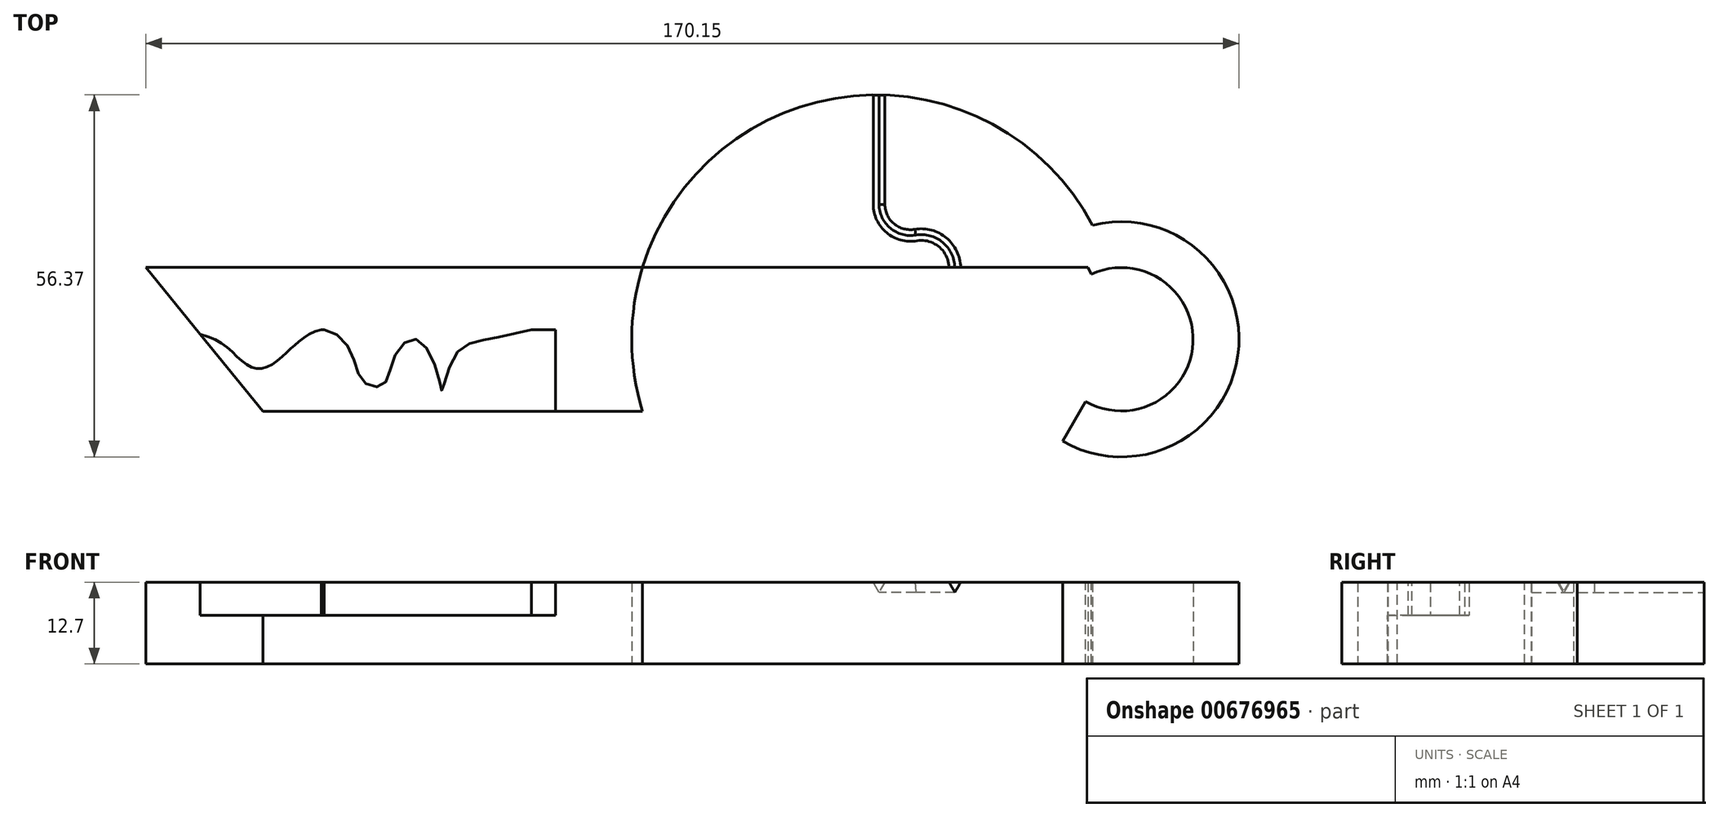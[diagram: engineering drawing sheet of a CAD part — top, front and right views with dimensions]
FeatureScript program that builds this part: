
annotation { "Feature Type Name" : "Feature", "Feature Type Description" : "" }
export const myFeature = defineFeature(function(context is Context, id is Id, definition is map)
    precondition{}
    {
        {
            var Q0;
            Q0=qCreatedBy(makeId("Top.planeOp"),FACE);
            var sketch = newSketch(context, id + "F0", { "sketchPlane" : qUnion([Q0])});
            skLineSegment(sketch, "E0", {"start": v(-76.55, 0) * mm, "end": v(76.12, 0) * mm});
            skLineSegment(sketch, "E1", {"start": v(0, 77.38) * mm, "end": v(0, -75.9) * mm});
            skLineSegment(sketch, "E2", {"start": v(0, 0) * mm, "end": v(76.12, 0) * mm});
            skLineSegment(sketch, "E3", {"start": v(38.06, 0) * mm, "end": v(38.06, 75.69) * mm});
            skCircle(sketch, "E4", {"center": v(38.06, 0) * mm, "radius": 38.06 * mm});
            skLineSegment(sketch, "E5.bottom", {"start": v(-75.64, 11.2) * mm, "end": v(74.43, 11.2) * mm});
            skLineSegment(sketch, "E5.top", {"start": v(-75.64, -11.2) * mm, "end": v(1.69, -11.2) * mm});
            skLineSegment(sketch, "E5.left", {"start": v(-75.64, 11.2) * mm, "end": v(-75.64, -11.2) * mm});
            skPoint(sketch, "E5.middle", {"position": v(0, 0) * mm});
            skSolve(sketch);
        }
        {
            var Q0;
            {var subQ0=sQuery(id+"F0.wireOp",EDGE,"E4");var subQ1=sQuery(id+"F0.wireOp",EDGE,"E3");var subQ2=makeQuery(id+"F0.imprint","INTERSECT",VERTEX,{"derivedFrom":[subQ1,subQ0]});Q0=makeQuery(id+"F0.imprint","IMPRINT",FACE,{"disambiguationData":[TD([[makeQuery(id+"F0.imprint","IMPRINT",EDGE,{"disambiguationData":[TD([[subQ2,1.0]])],"derivedFrom":subQ1}),1.0]])]});}
            var Q1;
            {var subQ0=sQuery(id+"F0.wireOp",EDGE,"E4");var subQ1=sQuery(id+"F0.wireOp",EDGE,"E3");var subQ2=makeQuery(id+"F0.imprint","INTERSECT",VERTEX,{"derivedFrom":[subQ1,subQ0]});Q1=makeQuery(id+"F0.imprint","IMPRINT",FACE,{"disambiguationData":[TD([[makeQuery(id+"F0.imprint","IMPRINT",EDGE,{"disambiguationData":[TD([[subQ2,1.0]])],"derivedFrom":subQ1}),-1.0]])]});}
            var Q2;
            {var subQ0=sQuery(id+"F0.wireOp",EDGE,"E4");var subQ1=sQuery(id+"F0.wireOp",EDGE,"E2");var subQ2=makeQuery(id+"F0.imprint","INTERSECT",VERTEX,{"derivedFrom":[subQ1,subQ0]});Q2=makeQuery(id+"F0.imprint","IMPRINT",FACE,{"disambiguationData":[TD([[makeQuery(id+"F0.imprint","IMPRINT",EDGE,{"disambiguationData":[TD([[subQ2,1.0]])],"derivedFrom":subQ1}),1.0]])]});}
            var Q3;
            {var subQ1=sQuery(id+"F0.wireOp",EDGE,"E2");var subQ3=sQuery(id+"F0.wireOp",EDGE,"E3");var subQ4=makeQuery(id+"F0.imprint","INTERSECT",VERTEX,{"derivedFrom":[subQ1,subQ3]});Q3=makeQuery(id+"F0.imprint","IMPRINT",FACE,{"disambiguationData":[TD([[makeQuery(id+"F0.imprint","IMPRINT",EDGE,{"disambiguationData":[TD([[subQ4,-1.0]])],"derivedFrom":subQ3}),1.0]])]});}
            var Q4;
            {var subQ0=sQuery(id+"F0.wireOp",EDGE,"E4");var subQ1=sQuery(id+"F0.wireOp",EDGE,"E2");var subQ4=makeQuery(id+"F0.imprint","INTERSECT",VERTEX,{"derivedFrom":[subQ1,subQ0]});Q4=makeQuery(id+"F0.imprint","IMPRINT",FACE,{"disambiguationData":[TD([[makeQuery(id+"F0.imprint","IMPRINT",EDGE,{"disambiguationData":[TD([[subQ4,1.0]])],"derivedFrom":subQ1}),-1.0]])]});}
            var Q5;
            {var subQ3=sQuery(id+"F0.wireOp",EDGE,"E5.left");var subQ5=sQuery(id+"F0.wireOp",EDGE,"E5.top");var subQ6=makeQuery(id+"F0.imprint","INTERSECT",VERTEX,{"derivedFrom":[subQ5,subQ3]});Q5=makeQuery(id+"F0.imprint","IMPRINT",FACE,{"disambiguationData":[TD([[makeQuery(id+"F0.imprint","IMPRINT",EDGE,{"disambiguationData":[TD([[subQ6,-1.0]])],"derivedFrom":subQ5}),1.0]])]});}
            var Q6;
            {var subQ3=sQuery(id+"F0.wireOp",EDGE,"E5.left");var subQ5=sQuery(id+"F0.wireOp",EDGE,"E5.bottom");var subQ7=makeQuery(id+"F0.imprint","INTERSECT",VERTEX,{"derivedFrom":[subQ5,subQ3]});Q6=makeQuery(id+"F0.imprint","IMPRINT",FACE,{"disambiguationData":[TD([[makeQuery(id+"F0.imprint","IMPRINT",EDGE,{"disambiguationData":[TD([[subQ7,-1.0]])],"derivedFrom":subQ5}),-1.0]])]});}
            var Q7;
            {var subQ1=sQuery(id+"F0.wireOp",EDGE,"E1");var subQ3=sQuery(id+"F0.wireOp",EDGE,"E5.bottom");var subQ4=makeQuery(id+"F0.imprint","INTERSECT",VERTEX,{"derivedFrom":[subQ1,subQ3]});Q7=makeQuery(id+"F0.imprint","IMPRINT",FACE,{"disambiguationData":[TD([[makeQuery(id+"F0.imprint","IMPRINT",EDGE,{"disambiguationData":[TD([[subQ4,-1.0]])],"derivedFrom":subQ3}),-1.0]])]});}
            var Q8;
            {var subQ0=sQuery(id+"F0.wireOp",EDGE,"E4");var subQ3=sQuery(id+"F0.wireOp",EDGE,"E5.top");var subQ5=makeQuery(id+"F0.imprint","INTERSECT",VERTEX,{"derivedFrom":[subQ0,subQ3]});Q8=makeQuery(id+"F0.imprint","IMPRINT",FACE,{"disambiguationData":[TD([[makeQuery(id+"F0.imprint","IMPRINT",EDGE,{"disambiguationData":[TD([[subQ5,1.0]])],"derivedFrom":subQ3}),1.0]])]});}
            extrude(context, id + "F1", {"entities" : qUnion([Q0, Q1, Q2, Q3, Q4, Q5, Q6, Q7, Q8]), "depth" : 12.7 * mm, "offsetDistance" : 25.4 * mm});
        }
        {
            var Q0;
            Q0=makeQuery(id+"F1.opExtrude","SWEPT_FACE",FACE,{"disambiguationData":[OSD([sQuery(id+"F0.wireOp",EDGE,"E5.top")])]});
            var sketch = newSketch(context, id + "F2", { "sketchPlane" : qUnion([Q0])});
            skPoint(sketch, "E6.oppositeSnap0", {"position": v(1.69, 6.35) * mm});
            skLineSegment(sketch, "E7.bottom", {"start": v(-75.64, 12.7) * mm, "end": v(-11.84, 12.7) * mm});
            skLineSegment(sketch, "E7.top", {"start": v(-75.64, 7.53) * mm, "end": v(-11.84, 7.53) * mm});
            skLineSegment(sketch, "E7.left", {"start": v(-75.64, 12.7) * mm, "end": v(-75.64, 7.53) * mm});
            skLineSegment(sketch, "E7.right", {"start": v(-11.84, 12.7) * mm, "end": v(-11.84, 7.53) * mm});
            skSolve(sketch);
        }
        {
            var Q0;
            Q0 = qSketchRegion(id + "F2", true);
            extrude(context, id + "F3", {"entities" : qUnion([Q0]), "operationType" : NewBodyOperationType.REMOVE, "oppositeDirection" : true, "depth" : 12.7 * mm, "offsetDistance" : 25.4 * mm});
        }
        {
            var Q0;
            Q0=makeQuery(id+"F3.boolean.opBoolean","COPY",FACE,{"derivedFrom":makeQuery(id+"F3.opExtrude","SWEPT_FACE",FACE,{"disambiguationData":[OSD([sQuery(id+"F2.wireOp",EDGE,"E7.top")])]})});
            var sketch = newSketch(context, id + "F4", { "sketchPlane" : qUnion([Q0])});
            skPoint(sketch, "E8.8.internal.snap0", {"position": v(-43.74, 1.5) * mm});
            skFitSpline(sketch, "E8", {"points": [v(-71.4, 1.5) * mm, v(-64.86, 0) * mm, v(-61.37, -2.73) * mm, v(-58.75, -4.47) * mm, v(-56.14, -4.03) * mm, v(-53.52, -1.85) * mm, v(-51.34, 0) * mm, v(-47.85, 1.5) * mm, v(-43.74, -1.85) * mm, v(-41.75, -6.65) * mm, v(-38.7, -7.09) * mm, v(-36.95, -2.73) * mm, v(-33.46, 0) * mm, v(-29.98, -6.21) * mm, v(-29.54, -7.96) * mm, v(-27.36, -2.29) * mm, v(-22.56, 0) * mm, v(-15.59, 1.5) * mm], "startDerivative": vector(98.42, -12.85) * mm, "endDerivative": vector(95.91, 21.9) * mm});
            skLineSegment(sketch, "E9", {"start": v(-71.4, 1.5) * mm, "end": v(-15.59, 1.5) * mm});
            skSolve(sketch);
        }
        {
            var Q0;
            {var subQ0=sQuery(id+"F4.wireOp",EDGE,"E9");var subQ1=sQuery(id+"F4.wireOp",EDGE,"E8");var subQ3=makeQuery(id+"F4.imprint","INTERSECT",VERTEX,{"disambiguationData":[OD(0.0)],"derivedFrom":[subQ1,subQ0]});Q0=makeQuery(id+"F4.imprint","IMPRINT",FACE,{"disambiguationData":[TD([[makeQuery(id+"F4.imprint","IMPRINT",EDGE,{"disambiguationData":[TD([[subQ3,1.0]])],"derivedFrom":subQ1}),1.0]])]});}
            var Q1;
            {var subQ0=sQuery(id+"F4.wireOp",EDGE,"E9");var subQ1=sQuery(id+"F4.wireOp",EDGE,"E8");var subQ3=makeQuery(id+"F4.imprint","INTERSECT",VERTEX,{"disambiguationData":[OD(1.0)],"derivedFrom":[subQ1,subQ0]});Q1=makeQuery(id+"F4.imprint","IMPRINT",FACE,{"disambiguationData":[TD([[makeQuery(id+"F4.imprint","IMPRINT",EDGE,{"disambiguationData":[TD([[subQ3,-1.0]])],"derivedFrom":subQ1}),1.0]])]});}
            var Q2;
            Q2=makeQuery(id+"F1.opExtrude","CAP_FACE",FACE,{"disambiguationData":[OSD([sQuery(id+"F0.wireOp",EDGE,"E4"),sQuery(id+"F0.wireOp",EDGE,"E5.bottom"),sQuery(id+"F0.wireOp",EDGE,"E5.top"),sQuery(id+"F0.wireOp",EDGE,"E5.left")])],"isStart":false});
            extrude(context, id + "F5", {"entities" : qUnion([Q0, Q1]), "operationType" : NewBodyOperationType.ADD, "endBound" : BoundingType.UP_TO_SURFACE, "depth" : 25.4 * mm, "endBoundEntityFace" : qUnion([Q2]), "offsetDistance" : 25.4 * mm});
        }
        {
            var Q0;
            {var subQ0=sQuery(id+"F0.wireOp",EDGE,"E5.left");var subQ1=sQuery(id+"F0.wireOp",EDGE,"E5.top");var subQ2=sQuery(id+"F0.wireOp",EDGE,"E5.bottom");var subQ3=sQuery(id+"F0.wireOp",EDGE,"E4");Q0=makeQuery(id+"F5.boolean.opBoolean","MERGE",FACE,{"derivedFrom":[makeQuery(id+"F1.opExtrude","CAP_FACE",FACE,{"disambiguationData":[OSD([subQ3,subQ2,subQ1,subQ0])],"isStart":false}),makeQuery(id+"F5.opExtrude","CAP_FACE",FACE,{"disambiguationData":[OSD([subQ3,subQ2,subQ1,subQ0]),OD(0.0)],"isStart":false}),makeQuery(id+"F5.opExtrude","CAP_FACE",FACE,{"disambiguationData":[OSD([subQ3,subQ2,subQ1,subQ0]),OD(1.0)],"isStart":false})]});}
            var sketch = newSketch(context, id + "F6", { "sketchPlane" : qUnion([Q0])});
            skLineSegment(sketch, "E10", {"start": v(-54.4, -14.93) * mm, "end": v(-80.56, -12.75) * mm});
            skLineSegment(sketch, "E11", {"start": v(-80.56, -12.75) * mm, "end": v(-75.64, 11.2) * mm});
            skLineSegment(sketch, "E12", {"start": v(-75.64, 11.2) * mm, "end": v(-54.4, -14.93) * mm});
            skSolve(sketch);
        }
        {
            var Q0;
            Q0 = qSketchRegion(id + "F6", true);
            extrude(context, id + "F7", {"entities" : qUnion([Q0]), "operationType" : NewBodyOperationType.REMOVE, "endBound" : BoundingType.THROUGH_ALL, "oppositeDirection" : true, "depth" : 25.4 * mm, "offsetDistance" : 25.4 * mm});
        }
        {
            var Q0;
            Q0=qCreatedBy(makeId("Right.planeOp"),FACE);
            cPlane(context, id + "F8", {"entities" : qUnion([Q0]), "cplaneType" : CPlaneType.OFFSET, "offset" : 76.2 * mm, "width" : 152.4 * mm, "height" : 152.4 * mm});
        }
        {
            var Q0;
            Q0=qCreatedBy(id+"F8.planeOp",FACE);
            var sketch = newSketch(context, id + "F9", { "sketchPlane" : qUnion([Q0])});
            skLineSegment(sketch, "E13", {"start": v(0, -5.67) * mm, "end": v(0, 19.48) * mm});
            skLineSegment(sketch, "E14.top", {"start": v(11.16, 0) * mm, "end": v(18.3, 0) * mm});
            skLineSegment(sketch, "E15", {"start": v(11.16, 0) * mm, "end": v(11.16, 12.7) * mm});
            skLineSegment(sketch, "E16", {"start": v(11.16, 12.7) * mm, "end": v(18.3, 12.7) * mm});
            skLineSegment(sketch, "E17", {"start": v(18.3, 12.7) * mm, "end": v(18.3, 0) * mm});
            skSolve(sketch);
        }
        {
            var Q0;
            Q0=makeQuery(id+"F9.imprint","IMPRINT",FACE,{"disambiguationData":[TD([[makeQuery(id+"F9.imprint","IMPRINT",EDGE,{"derivedFrom":sQuery(id+"F9.wireOp",EDGE,"E14.top")}),1.0]])]});
            var Q1;
            Q1=sQuery(id+"F9.wireOp",EDGE,"E13");
            revolve(context, id + "F10", {"operationType" : NewBodyOperationType.ADD, "entities" : qUnion([Q0]), "axis" : qUnion([Q1]), "revolveType" : RevolveType.TWO_DIRECTIONS, "angle" : 25 * degree, "angleBack" : 150 * degree});
        }
        {
            var Q0;
            Q0=qCreatedBy(makeId("Front.planeOp"),FACE);
            cPlane(context, id + "F11", {"entities" : qUnion([Q0]), "cplaneType" : CPlaneType.OFFSET, "offset" : 38.1 * mm, "width" : 152.4 * mm, "height" : 152.4 * mm});
        }
        {
            var Q0;
            {var subQ0=sQuery(id+"F0.wireOp",EDGE,"E5.left");var subQ1=sQuery(id+"F0.wireOp",EDGE,"E5.top");var subQ2=sQuery(id+"F0.wireOp",EDGE,"E5.bottom");var subQ3=sQuery(id+"F0.wireOp",EDGE,"E4");Q0=makeQuery(id+"F5.boolean.opBoolean","MERGE",FACE,{"derivedFrom":[makeQuery(id+"F1.opExtrude","CAP_FACE",FACE,{"disambiguationData":[OSD([subQ3,subQ2,subQ1,subQ0])],"isStart":false}),makeQuery(id+"F5.opExtrude","CAP_FACE",FACE,{"disambiguationData":[OSD([subQ3,subQ2,subQ1,subQ0]),OD(0.0)],"isStart":false}),makeQuery(id+"F5.opExtrude","CAP_FACE",FACE,{"disambiguationData":[OSD([subQ3,subQ2,subQ1,subQ0]),OD(1.0)],"isStart":false})]});}
            var sketch = newSketch(context, id + "F12", { "sketchPlane" : qUnion([Q0])});
            skLineSegment(sketch, "E18", {"start": v(38.5, -38.06) * mm, "end": v(38.5, -21.04) * mm});
            skArc(sketch, "E19", {"start": v(38.5, -21.04) * mm, "mid": v(40.22, -17.32) * mm, "end": v(44.17, -16.24) * mm});
            skArc(sketch, "E20", {"start": v(44.17, -16.24) * mm, "mid": v(48.62, -14.91) * mm, "end": v(50.28, -10.57) * mm});
            skLineSegment(sketch, "E21", {"start": v(50.28, -10.57) * mm, "end": v(50.28, 0) * mm});
            skLineSegment(sketch, "E22", {"start": v(0, 0) * mm, "end": v(43.3, 0) * mm});
            skLineSegment(sketch, "E23.MirrorCS", {"start": v(50.28, 10.57) * mm, "end": v(50.28, 0) * mm});
            skArc(sketch, "E24.MirrorCS", {"start": v(44.17, 16.24) * mm, "mid": v(48.62, 14.91) * mm, "end": v(50.28, 10.57) * mm});
            skArc(sketch, "E25.MirrorCS", {"start": v(38.5, 21.04) * mm, "mid": v(40.22, 17.32) * mm, "end": v(44.17, 16.24) * mm});
            skLineSegment(sketch, "E26.MirrorCS", {"start": v(38.5, 38.06) * mm, "end": v(38.5, 21.04) * mm});
            skSolve(sketch);
        }
        {
            var Q0;
            Q0=qCreatedBy(id+"F11.planeOp",FACE);
            var sketch = newSketch(context, id + "F13", { "sketchPlane" : qUnion([Q0])});
            skCircle(sketch, "E27.cCircle", {"center": v(38.5, 12.73) * mm, "radius": 1.6 * mm, "construction": true});
            skLineSegment(sketch, "E27.0", {"start": v(38.5, 11.14) * mm, "end": v(37.1, 13.53) * mm});
            skLineSegment(sketch, "E27.1", {"start": v(37.1, 13.53) * mm, "end": v(39.87, 13.53) * mm});
            skLineSegment(sketch, "E27.2", {"start": v(39.87, 13.53) * mm, "end": v(38.5, 11.14) * mm});
            skSolve(sketch);
        }
        {
            var Q0;
            Q0=makeQuery(id+"F13.imprint","IMPRINT",FACE,{"disambiguationData":[TD([[makeQuery(id+"F13.imprint","IMPRINT",EDGE,{"derivedFrom":sQuery(id+"F13.wireOp",EDGE,"E27.0")}),-1.0]])]});
            var Q1;
            Q1=sQuery(id+"F12.wireOp",EDGE,"E18");
            var Q2;
            Q2=sQuery(id+"F12.wireOp",EDGE,"E19");
            var Q3;
            Q3=sQuery(id+"F12.wireOp",EDGE,"E20");
            var Q4;
            Q4=sQuery(id+"F12.wireOp",EDGE,"E21");
            var Q5;
            Q5=sQuery(id+"F12.wireOp",EDGE,"E23.MirrorCS");
            var Q6;
            Q6=sQuery(id+"F12.wireOp",EDGE,"E24.MirrorCS");
            var Q7;
            Q7=sQuery(id+"F12.wireOp",EDGE,"E25.MirrorCS");
            var Q8;
            Q8=sQuery(id+"F12.wireOp",EDGE,"E26.MirrorCS");
            sweep(context, id + "F14", {"operationType" : NewBodyOperationType.REMOVE, "profiles" : qUnion([Q0]), "path" : qUnion([Q1, Q2, Q3, Q4, Q5, Q6, Q7, Q8])});
        }
    });
